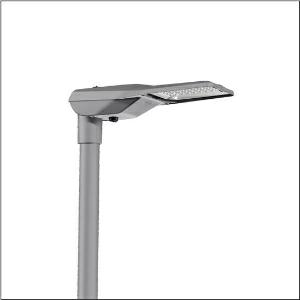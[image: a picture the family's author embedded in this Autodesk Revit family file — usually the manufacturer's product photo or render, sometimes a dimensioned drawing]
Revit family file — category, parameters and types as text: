
# Revit family: streetlight_sl_21_iq_mini___st0_5a_5xe2b31y08hb_0ff0
name_source: partatom
category: Lighting Fixtures
units: mm (PartAtom-declared; Revit-internal decimal feet)

## family parameters
Cut with Voids When Loaded = No
Host = Face
Light Source = No
Part Type = Normal
Room Calculation Point = No
Round Connector Dimension = Use Diameter
Shared = No

## types (1)
- --- (1 x LED, 9750 lm, 71 W, 3000K)
    Apparent Load = 71 VA
    CIE Flux Codes = 41 75 97 100 100
    Color Rendering = 70
    Color Temperature = 3000K
    Default Elevation = 1800 mm
    Description = Streetlight SL 21 iQ mini, mast luminaire, primary light control with lens, of PMMA, primary optical cover: cover, of toughened safety glass, transparent, light distribution: ST0.5a, light emission: direct distribution, primary light characteristic: asymmetric, installation type: post-top, side-entry, LED, High Power LED, rated luminous flux: 9.750lm, luminous efficacy: 137lm/W, light colour: 730, colour temperature: 3000K, control: presetting dimming logarithmic, Street-Remote, Auto-Match, Temp-Guard, Lumen-Switch, Night-Set, Smart-Wire, Light-Fading, Desk-Remote (wireless, voltage-free reading and setting of iQ features in the workshop via application-optimized NFC function/RFID function), optimised constant luminous flux control (CLO 2.0), mains connection: 220..240V, AC, 50/60Hz, start of lifetime: 71W, end of service life: 75W, reduction: 30W, luminaire housing, of diecast aluminium, powder-coated, Siteco® metallic grey (DB 702S), corrosivity category C5 mid according to DIN EN ISO 12944, please order mast flange separately, inclination adjustable: 0°, 5°, 10°, 15°, sealing non-destructively replaceable, multi-level sealing system, length: 628mm, width: 235mm, height: 110mm, mast flange for spigot size: 42mm (side-entry): 5XC10008XM4, 60/48mm (side-entry/post-top): 5XC10108XM2, 76/60mm (side-entry/post-top): 5XC10108XM1, Smart Interface below and above, protection rating (complete): IP66, insulation class (complete): insulation class II (safety insulation), certification: CE, ENEC, ENEC+, VDE, impact resistance: IK09, permissible operating ambient temperature for outdoor applications: -40..+50°C, standard-compliant lighting for roads and squares, packaging unit: 1 piece

Light Distribution: ST0.5a
    Height = 110 mm
    Lamp = 1 x LED
    Lamp Light Flux = 9750 lm
    Lamp Power = 71 W
    Lamp count = 1
    Length = 625 mm
    Luminous efficacy = 137 lm/W
    Manufacturer = Siteco
    ModVariant = No
    Model = 5XE2B31Y08HB
    Number of Poles = 1
    OnlyDefault = Yes
    Power Factor = 1
    Product Name = Streetlight SL 21 iQ mini | ST0.5a
    Product group = mast luminaire | pylon top
    ProductGroupID = 6100
    Protection Class = Protection class II
    Protection Degree = IP 66
    RLX_Detail_Level = 1
    RLX_Emergency_Light_Flux = 0 lm
    RLX_Emergency_Type = 0
    RLX_Emergency_Type_DB = No
    RlxData = <blob elided: 103621 chars, md5=baa44e85>
    Socket = socket
    Standby Power = 0 W
    System Light Flux = 9750 lm
    System Power = 71 W
    Type Comments = factory setting: luminous flux: 100 % | dim-lin: 254 | 716 mA
    Type Image = l_1003514.jpg
    URL = http://relux.com
    VarID = @adj_064301
    Voltage = 0 V
    Weight = 0.00 kg
    Width = 234 mm

## geometry (parser evidence)
native form markers: Blend x4, Sweep x11
no freeform markers — native parametric forms only
